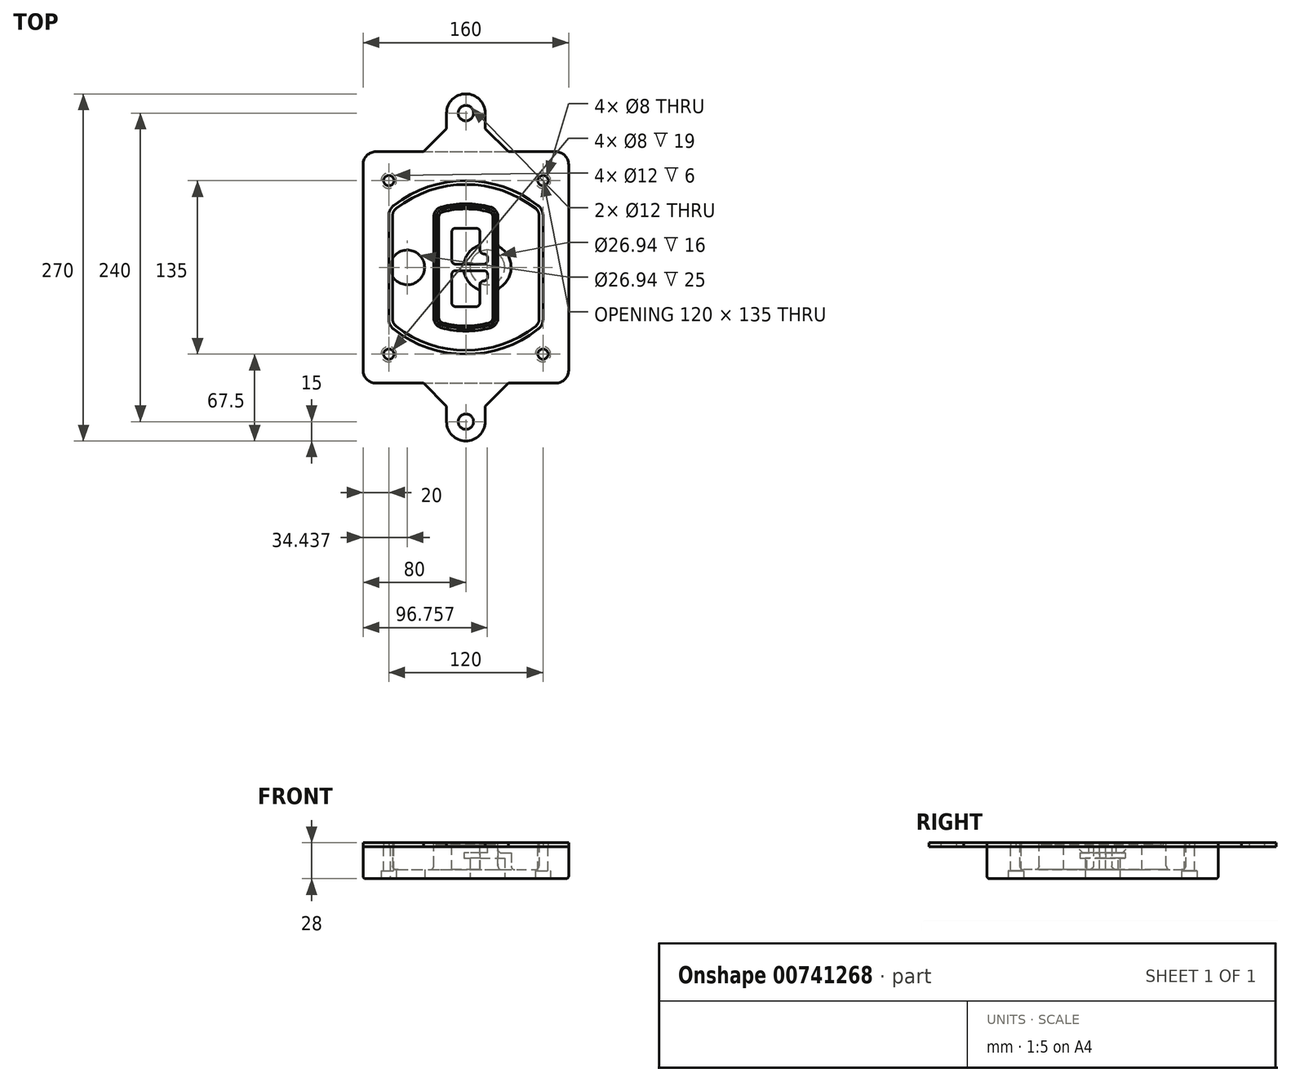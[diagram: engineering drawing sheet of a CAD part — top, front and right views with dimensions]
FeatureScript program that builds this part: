
annotation { "Feature Type Name" : "Feature", "Feature Type Description" : "" }
export const myFeature = defineFeature(function(context is Context, id is Id, definition is map)
    precondition{}
    {
        {
            var Q0;
            Q0=qCreatedBy(makeId("Top.planeOp"),FACE);
            var sketch = newSketch(context, id + "F0", { "sketchPlane" : qUnion([Q0])});
            skPoint(sketch, "E0.rect.middle", {"position": v(0, 0) * mm});
            skLineSegment(sketch, "E1.bottom", {"start": v(-70, -90) * mm, "end": v(70, -90) * mm});
            skLineSegment(sketch, "E1.top", {"start": v(-70, 90) * mm, "end": v(70, 90) * mm});
            skLineSegment(sketch, "E1.left", {"start": v(-80, -80) * mm, "end": v(-80, 80) * mm});
            skLineSegment(sketch, "E1.right", {"start": v(80, -80) * mm, "end": v(80, 80) * mm});
            skLineSegment(sketch, "E2", {"start": v(-80, 90) * mm, "end": v(80, -90) * mm, "construction": true});
            skLineSegment(sketch, "E3", {"start": v(80, 90) * mm, "end": v(-80, -90) * mm, "construction": true});
            skCircle(sketch, "E4", {"center": v(-60, 67.5) * mm, "radius": 4 * mm});
            skCircle(sketch, "E5", {"center": v(60, 67.5) * mm, "radius": 4 * mm});
            skCircle(sketch, "E6", {"center": v(60, -67.5) * mm, "radius": 4 * mm});
            skCircle(sketch, "E7", {"center": v(-60, -67.5) * mm, "radius": 4 * mm});
            skLineSegment(sketch, "E8", {"start": v(-60, 67.5) * mm, "end": v(60, 67.5) * mm, "construction": true});
            skLineSegment(sketch, "E9", {"start": v(60, 67.5) * mm, "end": v(60, -67.5) * mm, "construction": true});
            skLineSegment(sketch, "E10", {"start": v(60, -67.5) * mm, "end": v(-60, -67.5) * mm, "construction": true});
            skLineSegment(sketch, "E11", {"start": v(-60, -67.5) * mm, "end": v(-60, 67.5) * mm, "construction": true});
            skLineSegment(sketch, "E12", {"start": v(-60, 40.3) * mm, "end": v(-60, -40.3) * mm});
            skLineSegment(sketch, "E13", {"start": v(60, 40.3) * mm, "end": v(60, -40.3) * mm});
            skArc(sketch, "E14", {"start": v(56.15, 48.18) * mm, "mid": v(0, 67.5) * mm, "end": v(-56.15, 48.18) * mm});
            skArc(sketch, "E15", {"start": v(-56.15, -48.18) * mm, "mid": v(0, -67.5) * mm, "end": v(56.15, -48.18) * mm});
            skLineSegment(sketch, "E16", {"start": v(-60, 0) * mm, "end": v(60, 0) * mm, "construction": true});
            skPoint(sketch, "E17.visualSharp", {"position": v(-60, -45) * mm});
            skArc(sketch, "E17.filletArc", {"start": v(-60, -40.3) * mm, "mid": v(-58.99, -44.68) * mm, "end": v(-56.15, -48.18) * mm});
            skPoint(sketch, "E18.visualSharp", {"position": v(-60, 45) * mm});
            skArc(sketch, "E18.filletArc", {"start": v(-56.15, 48.18) * mm, "mid": v(-58.99, 44.68) * mm, "end": v(-60, 40.3) * mm});
            skPoint(sketch, "E19.visualSharp", {"position": v(60, 45) * mm});
            skArc(sketch, "E19.filletArc", {"start": v(60, 40.3) * mm, "mid": v(58.99, 44.68) * mm, "end": v(56.15, 48.18) * mm});
            skPoint(sketch, "E20.visualSharp", {"position": v(60, -45) * mm});
            skArc(sketch, "E20.filletArc", {"start": v(56.15, -48.18) * mm, "mid": v(58.99, -44.68) * mm, "end": v(60, -40.3) * mm});
            skPoint(sketch, "E21.visualSharp", {"position": v(-80, 90) * mm});
            skArc(sketch, "E21.filletArc", {"start": v(-70, 90) * mm, "mid": v(-77.07, 87.07) * mm, "end": v(-80, 80) * mm});
            skPoint(sketch, "E22.visualSharp", {"position": v(80, 90) * mm});
            skArc(sketch, "E22.filletArc", {"start": v(80, 80) * mm, "mid": v(77.07, 87.07) * mm, "end": v(70, 90) * mm});
            skPoint(sketch, "E23.visualSharp", {"position": v(80, -90) * mm});
            skArc(sketch, "E23.filletArc", {"start": v(70, -90) * mm, "mid": v(77.07, -87.07) * mm, "end": v(80, -80) * mm});
            skPoint(sketch, "E24.visualSharp", {"position": v(-80, -90) * mm});
            skArc(sketch, "E24.filletArc", {"start": v(-80, -80) * mm, "mid": v(-77.07, -87.07) * mm, "end": v(-70, -90) * mm});
            skArc(sketch, "E25.0", {"start": v(57, 40.3) * mm, "mid": v(56.3, 43.36) * mm, "end": v(54.3, 45.81) * mm});
            skLineSegment(sketch, "E25.1", {"start": v(57, 40.3) * mm, "end": v(57, -40.3) * mm});
            skArc(sketch, "E25.2", {"start": v(54.3, -45.81) * mm, "mid": v(56.3, -43.36) * mm, "end": v(57, -40.3) * mm});
            skArc(sketch, "E25.3", {"start": v(-54.3, -45.81) * mm, "mid": v(0, -64.5) * mm, "end": v(54.3, -45.81) * mm});
            skArc(sketch, "E25.4", {"start": v(-57, -40.3) * mm, "mid": v(-56.3, -43.36) * mm, "end": v(-54.3, -45.81) * mm});
            skArc(sketch, "E25.5", {"start": v(54.3, 45.81) * mm, "mid": v(0, 64.5) * mm, "end": v(-54.3, 45.81) * mm});
            skLineSegment(sketch, "E25.6", {"start": v(-57, 40.3) * mm, "end": v(-57, -40.3) * mm});
            skArc(sketch, "E25.7", {"start": v(-54.3, 45.81) * mm, "mid": v(-56.3, 43.36) * mm, "end": v(-57, 40.3) * mm});
            skArc(sketch, "E26.0", {"start": v(-58.62, 51.33) * mm, "mid": v(-62.58, 46.43) * mm, "end": v(-64, 40.3) * mm});
            skArc(sketch, "E26.1", {"start": v(58.62, 51.33) * mm, "mid": v(0, 71.5) * mm, "end": v(-58.62, 51.33) * mm});
            skArc(sketch, "E26.2", {"start": v(64, 40.3) * mm, "mid": v(62.58, 46.43) * mm, "end": v(58.62, 51.33) * mm});
            skLineSegment(sketch, "E26.3", {"start": v(64, 40.3) * mm, "end": v(64, -40.3) * mm});
            skArc(sketch, "E26.4", {"start": v(58.62, -51.33) * mm, "mid": v(62.58, -46.43) * mm, "end": v(64, -40.3) * mm});
            skLineSegment(sketch, "E26.5", {"start": v(-64, 40.3) * mm, "end": v(-64, -40.3) * mm});
            skArc(sketch, "E26.6", {"start": v(-58.62, -51.33) * mm, "mid": v(0, -71.5) * mm, "end": v(58.62, -51.33) * mm});
            skArc(sketch, "E26.7", {"start": v(-64, -40.3) * mm, "mid": v(-62.58, -46.43) * mm, "end": v(-58.62, -51.33) * mm});
            skSolve(sketch);
        }
        {
            var Q0;
            Q0=makeQuery(id+"F0.imprint","IMPRINT",FACE,{"disambiguationData":[TD([[makeQuery(id+"F0.imprint","IMPRINT",EDGE,{"derivedFrom":sQuery(id+"F0.wireOp",EDGE,"E1.bottom")}),1.0]])]});
            var Q1;
            Q1=makeQuery(id+"F0.imprint","IMPRINT",FACE,{"disambiguationData":[TD([[makeQuery(id+"F0.imprint","IMPRINT",EDGE,{"derivedFrom":sQuery(id+"F0.wireOp",EDGE,"E12")}),1.0]])]});
            var Q2;
            Q2=makeQuery(id+"F0.imprint","IMPRINT",FACE,{"disambiguationData":[TD([[makeQuery(id+"F0.imprint","IMPRINT",EDGE,{"derivedFrom":sQuery(id+"F0.wireOp",EDGE,"E25.0")}),1.0]])]});
            var Q3;
            Q3=makeQuery(id+"F0.imprint","IMPRINT",FACE,{"disambiguationData":[TD([[makeQuery(id+"F0.imprint","IMPRINT",EDGE,{"derivedFrom":sQuery(id+"F0.wireOp",EDGE,"E12")}),-1.0]])]});
            extrude(context, id + "F1", {"entities" : qUnion([Q0, Q1, Q2, Q3]), "oppositeDirection" : true, "depth" : 25 * mm});
        }
        {
            var Q0;
            Q0=makeQuery(id+"F0.imprint","IMPRINT",FACE,{"disambiguationData":[TD([[makeQuery(id+"F0.imprint","IMPRINT",EDGE,{"derivedFrom":sQuery(id+"F0.wireOp",EDGE,"E12")}),1.0]])]});
            extrude(context, id + "F2", {"entities" : qUnion([Q0]), "operationType" : NewBodyOperationType.ADD, "depth" : 3 * mm});
        }
        {
            var Q0;
            Q0=makeQuery(id+"F0.imprint","IMPRINT",FACE,{"disambiguationData":[TD([[makeQuery(id+"F0.imprint","IMPRINT",EDGE,{"derivedFrom":sQuery(id+"F0.wireOp",EDGE,"E25.0")}),1.0]])]});
            extrude(context, id + "F3", {"entities" : qUnion([Q0]), "operationType" : NewBodyOperationType.REMOVE, "oppositeDirection" : true, "depth" : 18 * mm});
        }
        {
            var Q0;
            Q0=makeQuery(id+"F2.opExtrude","CAP_FACE",FACE,{"disambiguationData":[OSD([sQuery(id+"F0.wireOp",EDGE,"E12"),sQuery(id+"F0.wireOp",EDGE,"E13"),sQuery(id+"F0.wireOp",EDGE,"E14"),sQuery(id+"F0.wireOp",EDGE,"E15"),sQuery(id+"F0.wireOp",EDGE,"E17.filletArc"),sQuery(id+"F0.wireOp",EDGE,"E18.filletArc"),sQuery(id+"F0.wireOp",EDGE,"E19.filletArc"),sQuery(id+"F0.wireOp",EDGE,"E20.filletArc"),sQuery(id+"F0.wireOp",EDGE,"E25.0"),sQuery(id+"F0.wireOp",EDGE,"E25.1"),sQuery(id+"F0.wireOp",EDGE,"E25.2"),sQuery(id+"F0.wireOp",EDGE,"E25.3"),sQuery(id+"F0.wireOp",EDGE,"E25.4"),sQuery(id+"F0.wireOp",EDGE,"E25.5"),sQuery(id+"F0.wireOp",EDGE,"E25.6"),sQuery(id+"F0.wireOp",EDGE,"E25.7")])],"isStart":false});
            var sketch = newSketch(context, id + "F4", { "sketchPlane" : qUnion([Q0])});
            skArc(sketch, "E27.0", {"start": v(-19.08, -46.97) * mm, "mid": v(0, -49.5) * mm, "end": v(19.08, -46.97) * mm});
            skArc(sketch, "E28.0", {"start": v(19.08, 46.97) * mm, "mid": v(0, 49.5) * mm, "end": v(-19.08, 46.97) * mm});
            skLineSegment(sketch, "E29", {"start": v(-25, 39.25) * mm, "end": v(-25, -39.25) * mm});
            skLineSegment(sketch, "E30", {"start": v(25, 39.25) * mm, "end": v(25, -39.25) * mm});
            skLineSegment(sketch, "E31", {"start": v(-25, 45.1) * mm, "end": v(25, 45.1) * mm, "construction": true});
            skLineSegment(sketch, "E32", {"start": v(-25, -45.1) * mm, "end": v(25, -45.1) * mm, "construction": true});
            skPoint(sketch, "E33.visualSharp", {"position": v(-25, 45.1) * mm});
            skArc(sketch, "E33.filletArc", {"start": v(-19.08, 46.97) * mm, "mid": v(-23.35, 44.11) * mm, "end": v(-25, 39.25) * mm});
            skPoint(sketch, "E34.visualSharp", {"position": v(25, 45.1) * mm});
            skArc(sketch, "E34.filletArc", {"start": v(25, 39.25) * mm, "mid": v(23.35, 44.11) * mm, "end": v(19.08, 46.97) * mm});
            skPoint(sketch, "E35.visualSharp", {"position": v(25, -45.1) * mm});
            skArc(sketch, "E35.filletArc", {"start": v(19.08, -46.97) * mm, "mid": v(23.35, -44.11) * mm, "end": v(25, -39.25) * mm});
            skPoint(sketch, "E36.visualSharp", {"position": v(-25, -45.1) * mm});
            skArc(sketch, "E36.filletArc", {"start": v(-25, -39.25) * mm, "mid": v(-23.35, -44.11) * mm, "end": v(-19.08, -46.97) * mm});
            skArc(sketch, "E37.0", {"start": v(54.3, 45.81) * mm, "mid": v(0, 64.5) * mm, "end": v(-54.3, 45.81) * mm});
            skArc(sketch, "E37.1", {"start": v(-54.3, 45.81) * mm, "mid": v(-56.3, 43.36) * mm, "end": v(-57, 40.3) * mm});
            skLineSegment(sketch, "E37.2", {"start": v(-57, 40.3) * mm, "end": v(-57, -40.3) * mm});
            skArc(sketch, "E37.3", {"start": v(-57, -40.3) * mm, "mid": v(-56.3, -43.36) * mm, "end": v(-54.3, -45.81) * mm});
            skArc(sketch, "E37.4", {"start": v(-54.3, -45.81) * mm, "mid": v(0, -64.5) * mm, "end": v(54.3, -45.81) * mm});
            skArc(sketch, "E37.5", {"start": v(54.3, -45.81) * mm, "mid": v(56.3, -43.36) * mm, "end": v(57, -40.3) * mm});
            skLineSegment(sketch, "E37.6", {"start": v(57, 40.3) * mm, "end": v(57, -40.3) * mm});
            skArc(sketch, "E37.7", {"start": v(57, 40.3) * mm, "mid": v(56.3, 43.36) * mm, "end": v(54.3, 45.81) * mm});
            skLineSegment(sketch, "E38.0", {"start": v(23, 39.25) * mm, "end": v(23, -39.25) * mm});
            skArc(sketch, "E38.1", {"start": v(18.56, -45.04) * mm, "mid": v(21.76, -42.9) * mm, "end": v(23, -39.25) * mm});
            skArc(sketch, "E38.2", {"start": v(-18.56, -45.04) * mm, "mid": v(0, -47.5) * mm, "end": v(18.56, -45.04) * mm});
            skArc(sketch, "E38.3", {"start": v(-23, -39.25) * mm, "mid": v(-21.76, -42.9) * mm, "end": v(-18.56, -45.04) * mm});
            skLineSegment(sketch, "E38.4", {"start": v(-23, 39.25) * mm, "end": v(-23, -39.25) * mm});
            skArc(sketch, "E38.5", {"start": v(23, 39.25) * mm, "mid": v(21.76, 42.9) * mm, "end": v(18.56, 45.04) * mm});
            skArc(sketch, "E38.6", {"start": v(-18.56, 45.04) * mm, "mid": v(-21.76, 42.9) * mm, "end": v(-23, 39.25) * mm});
            skArc(sketch, "E38.7", {"start": v(18.56, 45.04) * mm, "mid": v(0, 47.5) * mm, "end": v(-18.56, 45.04) * mm});
            skArc(sketch, "E39.0", {"start": v(21, 39.25) * mm, "mid": v(20.18, 41.68) * mm, "end": v(18.04, 43.1) * mm});
            skLineSegment(sketch, "E39.1", {"start": v(21, 39.25) * mm, "end": v(21, -39.25) * mm});
            skArc(sketch, "E39.2", {"start": v(18.04, -43.1) * mm, "mid": v(20.18, -41.68) * mm, "end": v(21, -39.25) * mm});
            skArc(sketch, "E39.3", {"start": v(-18.04, -43.1) * mm, "mid": v(0, -45.5) * mm, "end": v(18.04, -43.1) * mm});
            skArc(sketch, "E39.4", {"start": v(-21, -39.25) * mm, "mid": v(-20.18, -41.68) * mm, "end": v(-18.04, -43.1) * mm});
            skArc(sketch, "E39.5", {"start": v(18.04, 43.1) * mm, "mid": v(0, 45.5) * mm, "end": v(-18.04, 43.1) * mm});
            skLineSegment(sketch, "E39.6", {"start": v(-21, 39.25) * mm, "end": v(-21, -39.25) * mm});
            skArc(sketch, "E39.7", {"start": v(-18.04, 43.1) * mm, "mid": v(-20.18, 41.68) * mm, "end": v(-21, 39.25) * mm});
            skLineSegment(sketch, "E40", {"start": v(-25, 0) * mm, "end": v(25, 0) * mm, "construction": true});
            skLineSegment(sketch, "E41", {"start": v(-11, 5.5) * mm, "end": v(-11, 27.5) * mm});
            skLineSegment(sketch, "E42", {"start": v(-8, 30.5) * mm, "end": v(8, 30.5) * mm});
            skLineSegment(sketch, "E43", {"start": v(11, 27.5) * mm, "end": v(11, 13.5) * mm});
            skLineSegment(sketch, "E44", {"start": v(14, 10.5) * mm, "end": v(14, 10.5) * mm});
            skLineSegment(sketch, "E45", {"start": v(17, 7.5) * mm, "end": v(17, 5.5) * mm});
            skLineSegment(sketch, "E46", {"start": v(14, 2.5) * mm, "end": v(-8, 2.5) * mm});
            skPoint(sketch, "E47.visualSharp", {"position": v(-11, 30.5) * mm});
            skArc(sketch, "E47.filletArc", {"start": v(-8, 30.5) * mm, "mid": v(-10.12, 29.62) * mm, "end": v(-11, 27.5) * mm});
            skPoint(sketch, "E48.visualSharp", {"position": v(11, 30.5) * mm});
            skArc(sketch, "E48.filletArc", {"start": v(11, 27.5) * mm, "mid": v(10.12, 29.62) * mm, "end": v(8, 30.5) * mm});
            skPoint(sketch, "E49.visualSharp", {"position": v(11, 10.5) * mm});
            skArc(sketch, "E49.filletArc", {"start": v(11, 13.5) * mm, "mid": v(11.88, 11.38) * mm, "end": v(14, 10.5) * mm});
            skPoint(sketch, "E50.visualSharp", {"position": v(17, 10.5) * mm});
            skArc(sketch, "E50.filletArc", {"start": v(17, 7.5) * mm, "mid": v(16.12, 9.62) * mm, "end": v(14, 10.5) * mm});
            skPoint(sketch, "E51.visualSharp", {"position": v(17, 2.5) * mm});
            skArc(sketch, "E51.filletArc", {"start": v(14, 2.5) * mm, "mid": v(16.12, 3.38) * mm, "end": v(17, 5.5) * mm});
            skPoint(sketch, "E52.visualSharp", {"position": v(-11, 2.5) * mm});
            skArc(sketch, "E52.filletArc", {"start": v(-11, 5.5) * mm, "mid": v(-10.12, 3.38) * mm, "end": v(-8, 2.5) * mm});
            skLineSegment(sketch, "E53.0.MirrorCS", {"start": v(14, -2.5) * mm, "end": v(-8, -2.5) * mm});
            skArc(sketch, "E54.0.MirrorCS", {"start": v(-11, -5.5) * mm, "mid": v(-10.12, -3.38) * mm, "end": v(-8, -2.5) * mm});
            skLineSegment(sketch, "E55.0.MirrorCS", {"start": v(-11, -5.5) * mm, "end": v(-11, -27.5) * mm});
            skArc(sketch, "E56.0.MirrorCS", {"start": v(-8, -30.5) * mm, "mid": v(-10.12, -29.62) * mm, "end": v(-11, -27.5) * mm});
            skLineSegment(sketch, "E57.0.MirrorCS", {"start": v(-8, -30.5) * mm, "end": v(8, -30.5) * mm});
            skArc(sketch, "E58.0.MirrorCS", {"start": v(11, -27.5) * mm, "mid": v(10.12, -29.62) * mm, "end": v(8, -30.5) * mm});
            skLineSegment(sketch, "E59.0.MirrorCS", {"start": v(11, -27.5) * mm, "end": v(11, -13.5) * mm});
            skArc(sketch, "E60.0.MirrorCS", {"start": v(11, -13.5) * mm, "mid": v(11.88, -11.38) * mm, "end": v(14, -10.5) * mm});
            skArc(sketch, "E61.0.MirrorCS", {"start": v(17, -7.5) * mm, "mid": v(16.12, -9.62) * mm, "end": v(14, -10.5) * mm});
            skLineSegment(sketch, "E62.0.MirrorCS", {"start": v(17, -7.5) * mm, "end": v(17, -5.5) * mm});
            skArc(sketch, "E63.0.MirrorCS", {"start": v(14, -2.5) * mm, "mid": v(16.12, -3.38) * mm, "end": v(17, -5.5) * mm});
            skSolve(sketch);
        }
        {
            var Q0;
            Q0=makeQuery(id+"F4.imprint","IMPRINT",FACE,{"disambiguationData":[TD([[makeQuery(id+"F4.imprint","IMPRINT",EDGE,{"derivedFrom":sQuery(id+"F4.wireOp",EDGE,"E27.0")}),1.0]])]});
            var Q1;
            Q1=makeQuery(id+"F4.imprint","IMPRINT",FACE,{"disambiguationData":[TD([[makeQuery(id+"F4.imprint","IMPRINT",EDGE,{"derivedFrom":sQuery(id+"F4.wireOp",EDGE,"E38.0")}),-1.0]])]});
            var Q2;
            Q2=makeQuery(id+"F4.imprint","IMPRINT",FACE,{"disambiguationData":[TD([[makeQuery(id+"F4.imprint","IMPRINT",EDGE,{"derivedFrom":sQuery(id+"F4.wireOp",EDGE,"E39.0")}),1.0]])]});
            extrude(context, id + "F5", {"entities" : qUnion([Q0, Q1, Q2]), "operationType" : NewBodyOperationType.ADD, "endBound" : BoundingType.UP_TO_NEXT, "oppositeDirection" : true, "depth" : 25 * mm});
        }
        {
            var Q0;
            Q0=makeQuery(id+"F4.imprint","IMPRINT",FACE,{"disambiguationData":[TD([[makeQuery(id+"F4.imprint","IMPRINT",EDGE,{"derivedFrom":sQuery(id+"F4.wireOp",EDGE,"E38.0")}),-1.0]])]});
            extrude(context, id + "F6", {"entities" : qUnion([Q0]), "operationType" : NewBodyOperationType.REMOVE, "oppositeDirection" : true, "depth" : 2 * mm});
        }
        {
            var Q0;
            Q0=makeQuery(id+"F1.opExtrude","CAP_FACE",FACE,{"disambiguationData":[OSD([sQuery(id+"F0.wireOp",EDGE,"E1.bottom"),sQuery(id+"F0.wireOp",EDGE,"E1.top"),sQuery(id+"F0.wireOp",EDGE,"E1.left"),sQuery(id+"F0.wireOp",EDGE,"E1.right"),sQuery(id+"F0.wireOp",EDGE,"E4"),sQuery(id+"F0.wireOp",EDGE,"E5"),sQuery(id+"F0.wireOp",EDGE,"E6"),sQuery(id+"F0.wireOp",EDGE,"E7"),sQuery(id+"F0.wireOp",EDGE,"E21.filletArc"),sQuery(id+"F0.wireOp",EDGE,"E22.filletArc"),sQuery(id+"F0.wireOp",EDGE,"E23.filletArc"),sQuery(id+"F0.wireOp",EDGE,"E24.filletArc")])],"isStart":false});
            var sketch = newSketch(context, id + "F7", { "sketchPlane" : qUnion([Q0])});
            skCircle(sketch, "E64", {"center": v(16.76, 0) * mm, "radius": 13.47 * mm});
            skCircle(sketch, "E65", {"center": v(-45.56, 0) * mm, "radius": 13.47 * mm});
            skLineSegment(sketch, "E66", {"start": v(80, 0) * mm, "end": v(-80, 0) * mm});
            skCircle(sketch, "E67", {"center": v(16.76, 0) * mm, "radius": 18.47 * mm});
            skCircle(sketch, "E68", {"center": v(60, -67.5) * mm, "radius": 6 * mm});
            skCircle(sketch, "E69", {"center": v(-60, -67.5) * mm, "radius": 6 * mm});
            skCircle(sketch, "E70", {"center": v(-60, 67.5) * mm, "radius": 6 * mm});
            skCircle(sketch, "E71", {"center": v(60, 67.5) * mm, "radius": 6 * mm});
            skSolve(sketch);
        }
        {
            var Q0;
            {var subQ1=sQuery(id+"F7.wireOp",EDGE,"E66");var subQ4=sQuery(id+"F7.wireOp",EDGE,"E64");var subQ6=makeQuery(id+"F7.imprint","INTERSECT",VERTEX,{"disambiguationData":[OD(0.0)],"derivedFrom":[subQ4,subQ1]});Q0=makeQuery(id+"F7.imprint","IMPRINT",FACE,{"disambiguationData":[TD([[makeQuery(id+"F7.imprint","IMPRINT",EDGE,{"disambiguationData":[TD([[subQ6,-1.0]])],"derivedFrom":subQ4}),-1.0]])]});}
            var Q1;
            {var subQ0=sQuery(id+"F7.wireOp",EDGE,"E66");var subQ1=sQuery(id+"F7.wireOp",EDGE,"E64");var subQ3=makeQuery(id+"F7.imprint","INTERSECT",VERTEX,{"disambiguationData":[OD(0.0)],"derivedFrom":[subQ1,subQ0]});Q1=makeQuery(id+"F7.imprint","IMPRINT",FACE,{"disambiguationData":[TD([[makeQuery(id+"F7.imprint","IMPRINT",EDGE,{"disambiguationData":[TD([[subQ3,-1.0]])],"derivedFrom":subQ1}),1.0]])]});}
            var Q2;
            {var subQ0=sQuery(id+"F7.wireOp",EDGE,"E66");var subQ1=sQuery(id+"F7.wireOp",EDGE,"E64");var subQ3=makeQuery(id+"F7.imprint","INTERSECT",VERTEX,{"disambiguationData":[OD(0.0)],"derivedFrom":[subQ1,subQ0]});Q2=makeQuery(id+"F7.imprint","IMPRINT",FACE,{"disambiguationData":[TD([[makeQuery(id+"F7.imprint","IMPRINT",EDGE,{"disambiguationData":[TD([[subQ3,1.0]])],"derivedFrom":subQ1}),1.0]])]});}
            var Q3;
            {var subQ1=sQuery(id+"F7.wireOp",EDGE,"E66");var subQ4=sQuery(id+"F7.wireOp",EDGE,"E64");var subQ6=makeQuery(id+"F7.imprint","INTERSECT",VERTEX,{"disambiguationData":[OD(0.0)],"derivedFrom":[subQ4,subQ1]});Q3=makeQuery(id+"F7.imprint","IMPRINT",FACE,{"disambiguationData":[TD([[makeQuery(id+"F7.imprint","IMPRINT",EDGE,{"disambiguationData":[TD([[subQ6,1.0]])],"derivedFrom":subQ4}),-1.0]])]});}
            extrude(context, id + "F8", {"entities" : qUnion([Q0, Q1, Q2, Q3]), "operationType" : NewBodyOperationType.ADD, "oppositeDirection" : true, "depth" : 20 * mm});
        }
        {
            var Q0;
            {var subQ0=sQuery(id+"F7.wireOp",EDGE,"E66");var subQ1=sQuery(id+"F7.wireOp",EDGE,"E64");var subQ3=makeQuery(id+"F7.imprint","INTERSECT",VERTEX,{"disambiguationData":[OD(0.0)],"derivedFrom":[subQ1,subQ0]});Q0=makeQuery(id+"F7.imprint","IMPRINT",FACE,{"disambiguationData":[TD([[makeQuery(id+"F7.imprint","IMPRINT",EDGE,{"disambiguationData":[TD([[subQ3,-1.0]])],"derivedFrom":subQ1}),1.0]])]});}
            var Q1;
            {var subQ0=sQuery(id+"F7.wireOp",EDGE,"E66");var subQ1=sQuery(id+"F7.wireOp",EDGE,"E64");var subQ3=makeQuery(id+"F7.imprint","INTERSECT",VERTEX,{"disambiguationData":[OD(0.0)],"derivedFrom":[subQ1,subQ0]});Q1=makeQuery(id+"F7.imprint","IMPRINT",FACE,{"disambiguationData":[TD([[makeQuery(id+"F7.imprint","IMPRINT",EDGE,{"disambiguationData":[TD([[subQ3,1.0]])],"derivedFrom":subQ1}),1.0]])]});}
            extrude(context, id + "F9", {"entities" : qUnion([Q0, Q1]), "operationType" : NewBodyOperationType.REMOVE, "oppositeDirection" : true, "depth" : 16 * mm});
        }
        {
            var Q0;
            {var subQ0=sQuery(id+"F7.wireOp",EDGE,"E66");var subQ1=sQuery(id+"F7.wireOp",EDGE,"E65");var subQ3=makeQuery(id+"F7.imprint","INTERSECT",VERTEX,{"disambiguationData":[OD(0.0)],"derivedFrom":[subQ1,subQ0]});Q0=makeQuery(id+"F7.imprint","IMPRINT",FACE,{"disambiguationData":[TD([[makeQuery(id+"F7.imprint","IMPRINT",EDGE,{"disambiguationData":[TD([[subQ3,-1.0]])],"derivedFrom":subQ1}),1.0]])]});}
            var Q1;
            {var subQ0=sQuery(id+"F7.wireOp",EDGE,"E66");var subQ1=sQuery(id+"F7.wireOp",EDGE,"E65");var subQ3=makeQuery(id+"F7.imprint","INTERSECT",VERTEX,{"disambiguationData":[OD(0.0)],"derivedFrom":[subQ1,subQ0]});Q1=makeQuery(id+"F7.imprint","IMPRINT",FACE,{"disambiguationData":[TD([[makeQuery(id+"F7.imprint","IMPRINT",EDGE,{"disambiguationData":[TD([[subQ3,1.0]])],"derivedFrom":subQ1}),1.0]])]});}
            extrude(context, id + "F10", {"entities" : qUnion([Q0, Q1]), "operationType" : NewBodyOperationType.REMOVE, "oppositeDirection" : true, "depth" : 25 * mm});
        }
        {
            var Q0;
            Q0=makeQuery(id+"F7.imprint","IMPRINT",FACE,{"disambiguationData":[TD([[makeQuery(id+"F7.imprint","IMPRINT",EDGE,{"derivedFrom":sQuery(id+"F7.wireOp",EDGE,"E68")}),1.0]])]});
            var Q1;
            Q1=makeQuery(id+"F7.imprint","IMPRINT",FACE,{"disambiguationData":[TD([[makeQuery(id+"F7.imprint","IMPRINT",EDGE,{"derivedFrom":makeQuery(id+"F1.opExtrude","CAP_EDGE",EDGE,{"disambiguationData":[OSD([sQuery(id+"F0.wireOp",EDGE,"E5")])],"isStart":false})}),-1.0]])]});
            var Q2;
            Q2=makeQuery(id+"F7.imprint","IMPRINT",FACE,{"disambiguationData":[TD([[makeQuery(id+"F7.imprint","IMPRINT",EDGE,{"derivedFrom":sQuery(id+"F7.wireOp",EDGE,"E69")}),1.0]])]});
            var Q3;
            Q3=makeQuery(id+"F7.imprint","IMPRINT",FACE,{"disambiguationData":[TD([[makeQuery(id+"F7.imprint","IMPRINT",EDGE,{"derivedFrom":makeQuery(id+"F1.opExtrude","CAP_EDGE",EDGE,{"disambiguationData":[OSD([sQuery(id+"F0.wireOp",EDGE,"E4")])],"isStart":false})}),-1.0]])]});
            var Q4;
            Q4=makeQuery(id+"F7.imprint","IMPRINT",FACE,{"disambiguationData":[TD([[makeQuery(id+"F7.imprint","IMPRINT",EDGE,{"derivedFrom":sQuery(id+"F7.wireOp",EDGE,"E70")}),1.0]])]});
            var Q5;
            Q5=makeQuery(id+"F7.imprint","IMPRINT",FACE,{"disambiguationData":[TD([[makeQuery(id+"F7.imprint","IMPRINT",EDGE,{"derivedFrom":makeQuery(id+"F1.opExtrude","CAP_EDGE",EDGE,{"disambiguationData":[OSD([sQuery(id+"F0.wireOp",EDGE,"E7")])],"isStart":false})}),-1.0]])]});
            var Q6;
            Q6=makeQuery(id+"F7.imprint","IMPRINT",FACE,{"disambiguationData":[TD([[makeQuery(id+"F7.imprint","IMPRINT",EDGE,{"derivedFrom":sQuery(id+"F7.wireOp",EDGE,"E71")}),1.0]])]});
            var Q7;
            Q7=makeQuery(id+"F7.imprint","IMPRINT",FACE,{"disambiguationData":[TD([[makeQuery(id+"F7.imprint","IMPRINT",EDGE,{"derivedFrom":makeQuery(id+"F1.opExtrude","CAP_EDGE",EDGE,{"disambiguationData":[OSD([sQuery(id+"F0.wireOp",EDGE,"E6")])],"isStart":false})}),-1.0]])]});
            extrude(context, id + "F11", {"entities" : qUnion([Q0, Q1, Q2, Q3, Q4, Q5, Q6, Q7]), "operationType" : NewBodyOperationType.REMOVE, "oppositeDirection" : true, "depth" : 6 * mm});
        }
        {
            var Q0;
            Q0=makeQuery(id+"F9.boolean.opBoolean","COPY",FACE,{"derivedFrom":makeQuery(id+"F9.opExtrude","CAP_FACE",FACE,{"disambiguationData":[OSD([sQuery(id+"F7.wireOp",EDGE,"E64")])],"isStart":false})});
            var sketch = newSketch(context, id + "F12", { "sketchPlane" : qUnion([Q0])});
            skArc(sketch, "E72.0", {"start": v(11, 17.55) * mm, "mid": v(2.57, 11.82) * mm, "end": v(-1.54, 2.5) * mm});
            skArc(sketch, "E72.1", {"start": v(-1.54, -2.5) * mm, "mid": v(2.57, -11.82) * mm, "end": v(11, -17.55) * mm});
            skLineSegment(sketch, "E73", {"start": v(-1.54, -2.5) * mm, "end": v(14, -2.5) * mm});
            skLineSegment(sketch, "E74.0", {"start": v(14, 2.5) * mm, "end": v(-1.54, 2.5) * mm});
            skArc(sketch, "E74.1", {"start": v(14, 2.5) * mm, "mid": v(16.12, 3.38) * mm, "end": v(17, 5.5) * mm});
            skLineSegment(sketch, "E74.2", {"start": v(17, 7.5) * mm, "end": v(17, 5.5) * mm});
            skArc(sketch, "E74.3", {"start": v(17, 7.5) * mm, "mid": v(16.12, 9.62) * mm, "end": v(14, 10.5) * mm});
            skArc(sketch, "E74.4", {"start": v(11, 13.5) * mm, "mid": v(11.88, 11.38) * mm, "end": v(14, 10.5) * mm});
            skLineSegment(sketch, "E74.5", {"start": v(11, 17.55) * mm, "end": v(11, 13.5) * mm});
            skLineSegment(sketch, "E74.7", {"start": v(14, -2.5) * mm, "end": v(-1.54, -2.5) * mm});
            skArc(sketch, "E74.8", {"start": v(14, -2.5) * mm, "mid": v(16.12, -3.38) * mm, "end": v(17, -5.5) * mm});
            skLineSegment(sketch, "E74.9", {"start": v(17, -7.5) * mm, "end": v(17, -5.5) * mm});
            skArc(sketch, "E74.10", {"start": v(17, -7.5) * mm, "mid": v(16.12, -9.62) * mm, "end": v(14, -10.5) * mm});
            skArc(sketch, "E74.11", {"start": v(11, -13.5) * mm, "mid": v(11.88, -11.38) * mm, "end": v(14, -10.5) * mm});
            skLineSegment(sketch, "E74.12", {"start": v(11, -17.55) * mm, "end": v(11, -13.5) * mm});
            skPoint(sketch, "E75.orphan", {"position": v(11, -27.5) * mm});
            skPoint(sketch, "E76.orphan", {"position": v(-8, -2.5) * mm});
            skPoint(sketch, "E77.orphan", {"position": v(-8, 2.5) * mm});
            skPoint(sketch, "E78.orphan", {"position": v(11, 27.5) * mm});
            skSolve(sketch);
        }
        {
            var Q0;
            {var subQ7=sQuery(id+"F12.wireOp",EDGE,"E72.0");var subQ14=sQuery(id+"F12.wireOp",EDGE,"E72.1");var subQ16=sQuery(id+"F12.wireOp",EDGE,"E74.1");var subQ18=sQuery(id+"F12.wireOp",EDGE,"E74.8");Q0=qUnion([makeQuery(id+"F12.imprint","IMPRINT",FACE,{"disambiguationData":[TD([[makeQuery(id+"F12.imprint","IMPRINT",EDGE,{"derivedFrom":subQ7}),1.0]])]}),makeQuery(id+"F12.imprint","IMPRINT",FACE,{"disambiguationData":[TD([[makeQuery(id+"F12.imprint","IMPRINT",EDGE,{"derivedFrom":subQ14}),1.0]])]}),makeQuery(id+"F12.imprint","IMPRINT",FACE,{"disambiguationData":[TD([[makeQuery(id+"F12.imprint","IMPRINT",EDGE,{"derivedFrom":subQ16}),1.0]])]}),makeQuery(id+"F12.imprint","IMPRINT",FACE,{"disambiguationData":[TD([[makeQuery(id+"F12.imprint","IMPRINT",EDGE,{"derivedFrom":subQ18}),-1.0]])]})]);}
            var Q1;
            Q1=makeQuery(id+"F5.boolean.opBoolean","SPLIT",FACE,{"disambiguationData":[TD([makeQuery(id+"F5.opExtrude","SWEPT_FACE",FACE,{"disambiguationData":[OSD([sQuery(id+"F4.wireOp",EDGE,"E41")])]})])],"derivedFrom":makeQuery(id+"F3.boolean.opBoolean","COPY",FACE,{"derivedFrom":makeQuery(id+"F3.opExtrude","CAP_FACE",FACE,{"disambiguationData":[OSD([sQuery(id+"F0.wireOp",EDGE,"E25.0"),sQuery(id+"F0.wireOp",EDGE,"E25.1"),sQuery(id+"F0.wireOp",EDGE,"E25.2"),sQuery(id+"F0.wireOp",EDGE,"E25.3"),sQuery(id+"F0.wireOp",EDGE,"E25.4"),sQuery(id+"F0.wireOp",EDGE,"E25.5"),sQuery(id+"F0.wireOp",EDGE,"E25.6"),sQuery(id+"F0.wireOp",EDGE,"E25.7")])],"isStart":false})})});
            extrude(context, id + "F13", {"entities" : qUnion([Q0]), "operationType" : NewBodyOperationType.REMOVE, "endBound" : BoundingType.UP_TO_SURFACE, "endBoundEntityFace" : qUnion([Q1]), "depth" : 25 * mm});
        }
        {
            var Q0;
            Q0=makeQuery(id+"F3.boolean.opBoolean","COPY",EDGE,{"derivedFrom":makeQuery(id+"F3.opExtrude","CAP_EDGE",EDGE,{"disambiguationData":[OSD([sQuery(id+"F0.wireOp",EDGE,"E25.6")])],"isStart":false})});
            var Q1;
            Q1=makeQuery(id+"F8.boolean.opBoolean","INTERSECT",EDGE,{"derivedFrom":[makeQuery(id+"F5.opExtrude","SWEPT_FACE",FACE,{"disambiguationData":[OSD([sQuery(id+"F4.wireOp",EDGE,"E30")])]}),makeQuery(id+"F8.opExtrude","CAP_FACE",FACE,{"disambiguationData":[OSD([sQuery(id+"F7.wireOp",EDGE,"E67")])],"isStart":false})]});
            var Q2;
            Q2=makeQuery(id+"F8.boolean.opBoolean","INTERSECT",EDGE,{"disambiguationData":[OD(1.0)],"derivedFrom":[makeQuery(id+"F5.opExtrude","SWEPT_FACE",FACE,{"disambiguationData":[OSD([sQuery(id+"F4.wireOp",EDGE,"E30")])]}),makeQuery(id+"F8.opExtrude","SWEPT_FACE",FACE,{"disambiguationData":[OSD([sQuery(id+"F7.wireOp",EDGE,"E67")])]})]});
            var Q3;
            {var subQ0=sQuery(id+"F4.wireOp",EDGE,"E30");Q3=makeQuery(id+"F8.boolean.opBoolean","SPLIT",EDGE,{"disambiguationData":[TD([makeQuery(id+"F5.opExtrude","SWEPT_FACE",FACE,{"disambiguationData":[OSD([sQuery(id+"F4.wireOp",EDGE,"E35.filletArc")])]})])],"derivedFrom":makeQuery(id+"F5.opExtrude","CAP_EDGE",EDGE,{"disambiguationData":[OSD([subQ0])],"isStart":false})});}
            var Q4;
            {var subQ0=sQuery(id+"F0.wireOp",EDGE,"E25.7");var subQ1=sQuery(id+"F0.wireOp",EDGE,"E25.1");var subQ2=sQuery(id+"F0.wireOp",EDGE,"E25.6");var subQ3=sQuery(id+"F0.wireOp",EDGE,"E25.5");var subQ4=sQuery(id+"F0.wireOp",EDGE,"E25.4");var subQ5=sQuery(id+"F0.wireOp",EDGE,"E25.0");var subQ6=sQuery(id+"F0.wireOp",EDGE,"E25.2");var subQ7=sQuery(id+"F0.wireOp",EDGE,"E25.3");Q4=makeQuery(id+"F8.boolean.opBoolean","INTERSECT",EDGE,{"derivedFrom":[makeQuery(id+"F5.boolean.opBoolean","SPLIT",FACE,{"disambiguationData":[TD([makeQuery(id+"F2.opExtrude","SWEPT_FACE",FACE,{"disambiguationData":[OSD([subQ5])]})])],"derivedFrom":makeQuery(id+"F3.boolean.opBoolean","COPY",FACE,{"derivedFrom":makeQuery(id+"F3.opExtrude","CAP_FACE",FACE,{"disambiguationData":[OSD([subQ5,subQ1,subQ6,subQ7,subQ4,subQ3,subQ2,subQ0])],"isStart":false})})}),makeQuery(id+"F8.opExtrude","SWEPT_FACE",FACE,{"disambiguationData":[OSD([sQuery(id+"F7.wireOp",EDGE,"E67")])]})]});}
            var Q5;
            Q5=makeQuery(id+"F8.boolean.opBoolean","INTERSECT",EDGE,{"disambiguationData":[OD(0.0)],"derivedFrom":[makeQuery(id+"F5.opExtrude","SWEPT_FACE",FACE,{"disambiguationData":[OSD([sQuery(id+"F4.wireOp",EDGE,"E30")])]}),makeQuery(id+"F8.opExtrude","SWEPT_FACE",FACE,{"disambiguationData":[OSD([sQuery(id+"F7.wireOp",EDGE,"E67")])]})]});
            fillet(context, id + "F14", {"entities" : qUnion([Q0, Q1, Q2, Q3, Q4, Q5]), "radius" : 3 * mm, "tangentPropagation" : true, "allowEdgeOverflow" : false});
        }
        {
            var Q0;
            Q0=makeQuery(id+"F1.opExtrude","CAP_EDGE",EDGE,{"disambiguationData":[OSD([sQuery(id+"F0.wireOp",EDGE,"E1.bottom")])],"isStart":false});
            fillet(context, id + "F15", {"entities" : qUnion([Q0]), "radius" : 2 * mm, "tangentPropagation" : true, "allowEdgeOverflow" : false});
        }
        {
            var Q0;
            {var subQ0=sQuery(id+"F0.wireOp",EDGE,"E21.filletArc");var subQ1=sQuery(id+"F0.wireOp",EDGE,"E7");var subQ2=sQuery(id+"F0.wireOp",EDGE,"E6");var subQ3=sQuery(id+"F0.wireOp",EDGE,"E5");var subQ4=sQuery(id+"F0.wireOp",EDGE,"E4");var subQ5=sQuery(id+"F0.wireOp",EDGE,"E22.filletArc");var subQ6=sQuery(id+"F0.wireOp",EDGE,"E1.bottom");var subQ7=sQuery(id+"F0.wireOp",EDGE,"E1.right");var subQ8=sQuery(id+"F0.wireOp",EDGE,"E1.top");var subQ9=sQuery(id+"F0.wireOp",EDGE,"E1.left");var subQ10=sQuery(id+"F0.wireOp",EDGE,"E23.filletArc");var subQ11=sQuery(id+"F0.wireOp",EDGE,"E24.filletArc");Q0=makeQuery(id+"F2.boolean.opBoolean","SPLIT",FACE,{"disambiguationData":[TD([makeQuery(id+"F1.opExtrude","SWEPT_FACE",FACE,{"disambiguationData":[OSD([subQ6])]})])],"derivedFrom":makeQuery(id+"F1.opExtrude","CAP_FACE",FACE,{"disambiguationData":[OSD([subQ6,subQ8,subQ9,subQ7,subQ4,subQ3,subQ2,subQ1,subQ0,subQ5,subQ10,subQ11])],"isStart":true})});}
            var sketch = newSketch(context, id + "F16", { "sketchPlane" : qUnion([Q0])});
            skLineSegment(sketch, "E79", {"start": v(-33, 90) * mm, "end": v(-15, 108) * mm});
            skLineSegment(sketch, "E80", {"start": v(-15, 108) * mm, "end": v(-15, 120) * mm});
            skArc(sketch, "E81", {"start": v(15, 120) * mm, "mid": v(0, 135) * mm, "end": v(-15, 120) * mm});
            skLineSegment(sketch, "E82", {"start": v(15, 120) * mm, "end": v(15, 108) * mm});
            skLineSegment(sketch, "E83", {"start": v(15, 108) * mm, "end": v(33, 90) * mm});
            skCircle(sketch, "E84", {"center": v(0, 120) * mm, "radius": 6 * mm});
            skLineSegment(sketch, "E85", {"start": v(0, 90) * mm, "end": v(0, 120) * mm, "construction": true});
            skLineSegment(sketch, "E86", {"start": v(-80, 0) * mm, "end": v(80, 0) * mm, "construction": true});
            skLineSegment(sketch, "E87.MirrorCS", {"start": v(15, -108) * mm, "end": v(33, -90) * mm});
            skLineSegment(sketch, "E88.MirrorCS", {"start": v(0, -90) * mm, "end": v(0, -120) * mm, "construction": true});
            skArc(sketch, "E89.MirrorCS", {"start": v(15, -120) * mm, "mid": v(0, -135) * mm, "end": v(-15, -120) * mm});
            skLineSegment(sketch, "E90.MirrorCS", {"start": v(-33, -90) * mm, "end": v(-15, -108) * mm});
            skCircle(sketch, "E91.MirrorC", {"center": v(0, -120) * mm, "radius": 6 * mm});
            skLineSegment(sketch, "E92.MirrorCS", {"start": v(-15, -108) * mm, "end": v(-15, -120) * mm});
            skLineSegment(sketch, "E93.MirrorCS", {"start": v(15, -120) * mm, "end": v(15, -108) * mm});
            skLineSegment(sketch, "E94.0", {"start": v(-70, 90) * mm, "end": v(70, 90) * mm});
            skArc(sketch, "E94.1", {"start": v(80, 80) * mm, "mid": v(77.07, 87.07) * mm, "end": v(70, 90) * mm});
            skLineSegment(sketch, "E94.2", {"start": v(80, -80) * mm, "end": v(80, 80) * mm});
            skArc(sketch, "E94.3", {"start": v(70, -90) * mm, "mid": v(77.07, -87.07) * mm, "end": v(80, -80) * mm});
            skLineSegment(sketch, "E94.4", {"start": v(-70, -90) * mm, "end": v(70, -90) * mm});
            skCircle(sketch, "E94.5", {"center": v(60, -67.5) * mm, "radius": 4 * mm});
            skCircle(sketch, "E94.6", {"center": v(-60, -67.5) * mm, "radius": 4 * mm});
            skArc(sketch, "E94.7", {"start": v(-80, -80) * mm, "mid": v(-77.07, -87.07) * mm, "end": v(-70, -90) * mm});
            skLineSegment(sketch, "E94.8", {"start": v(-80, -80) * mm, "end": v(-80, 80) * mm});
            skArc(sketch, "E94.9", {"start": v(-70, 90) * mm, "mid": v(-77.07, 87.07) * mm, "end": v(-80, 80) * mm});
            skCircle(sketch, "E94.10", {"center": v(-60, 67.5) * mm, "radius": 4 * mm});
            skCircle(sketch, "E94.11", {"center": v(60, 67.5) * mm, "radius": 4 * mm});
            skArc(sketch, "E94.12", {"start": v(60, 40.3) * mm, "mid": v(58.99, 44.68) * mm, "end": v(56.15, 48.18) * mm});
            skLineSegment(sketch, "E94.13", {"start": v(60, 40.3) * mm, "end": v(60, -40.3) * mm});
            skArc(sketch, "E94.14", {"start": v(56.15, 48.18) * mm, "mid": v(0, 67.5) * mm, "end": v(-56.15, 48.18) * mm});
            skArc(sketch, "E94.15", {"start": v(-56.15, 48.18) * mm, "mid": v(-58.99, 44.68) * mm, "end": v(-60, 40.3) * mm});
            skLineSegment(sketch, "E94.16", {"start": v(-60, 40.3) * mm, "end": v(-60, -40.3) * mm});
            skArc(sketch, "E94.17", {"start": v(-60, -40.3) * mm, "mid": v(-58.99, -44.68) * mm, "end": v(-56.15, -48.18) * mm});
            skArc(sketch, "E94.18", {"start": v(-56.15, -48.18) * mm, "mid": v(0, -67.5) * mm, "end": v(56.15, -48.18) * mm});
            skArc(sketch, "E94.19", {"start": v(56.15, -48.18) * mm, "mid": v(58.99, -44.68) * mm, "end": v(60, -40.3) * mm});
            skSolve(sketch);
        }
        {
            var Q0;
            Q0 = qSketchRegion(id + "F16", true);
            var Q1;
            Q1=makeQuery(id+"F2.opExtrude","CAP_FACE",FACE,{"disambiguationData":[OSD([sQuery(id+"F0.wireOp",EDGE,"E12"),sQuery(id+"F0.wireOp",EDGE,"E13"),sQuery(id+"F0.wireOp",EDGE,"E14"),sQuery(id+"F0.wireOp",EDGE,"E15"),sQuery(id+"F0.wireOp",EDGE,"E17.filletArc"),sQuery(id+"F0.wireOp",EDGE,"E18.filletArc"),sQuery(id+"F0.wireOp",EDGE,"E19.filletArc"),sQuery(id+"F0.wireOp",EDGE,"E20.filletArc"),sQuery(id+"F0.wireOp",EDGE,"E25.0"),sQuery(id+"F0.wireOp",EDGE,"E25.1"),sQuery(id+"F0.wireOp",EDGE,"E25.2"),sQuery(id+"F0.wireOp",EDGE,"E25.3"),sQuery(id+"F0.wireOp",EDGE,"E25.4"),sQuery(id+"F0.wireOp",EDGE,"E25.5"),sQuery(id+"F0.wireOp",EDGE,"E25.6"),sQuery(id+"F0.wireOp",EDGE,"E25.7")])],"isStart":false});
            extrude(context, id + "F17", {"entities" : qUnion([Q0]), "endBound" : BoundingType.UP_TO_SURFACE, "depth" : 25 * mm, "endBoundEntityFace" : qUnion([Q1]), "offsetDistance" : 25 * mm});
        }
    });
